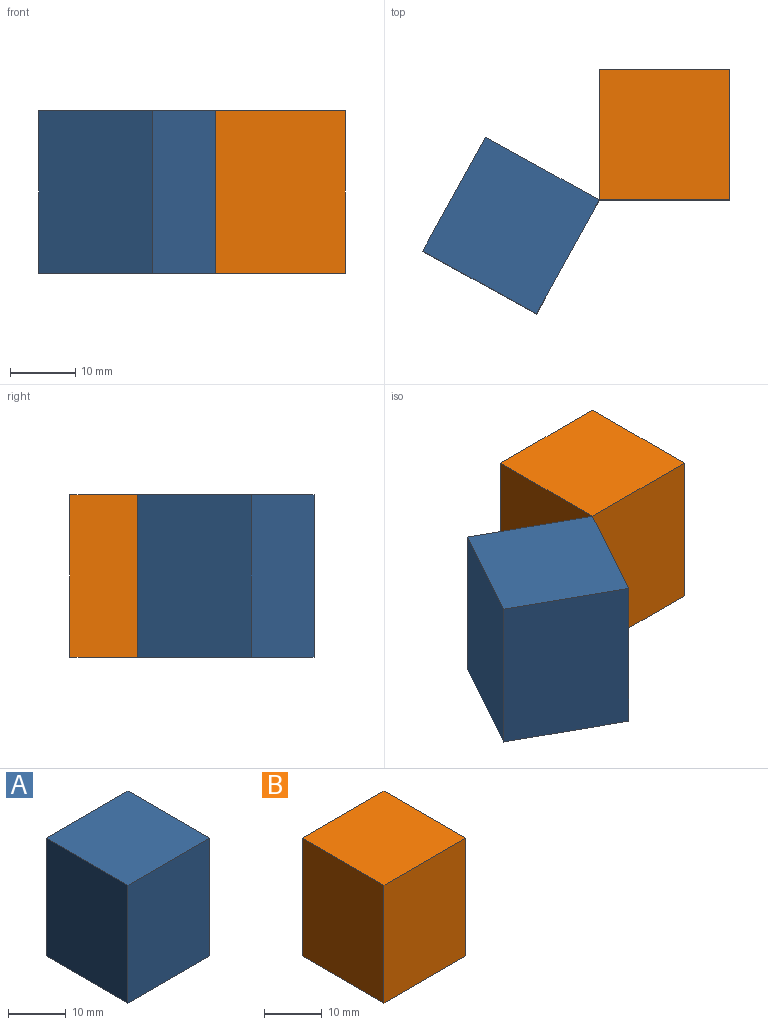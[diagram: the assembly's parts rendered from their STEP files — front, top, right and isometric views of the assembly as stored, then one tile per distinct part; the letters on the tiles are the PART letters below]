
ASSEMBLY  parts=2 mates=1
PART A: 6 faces, bbox 20x20x25 mm
  f0: plane 25x20mm, normal (1,0,0), area 500mm2, adj f1,f3,f4,f5
  f1: plane 25x20mm, normal (0,1,0), area 500mm2, adj f0,f2,f4,f5
  f2: plane 25x20mm, normal (-1,0,0), area 500mm2, adj f1,f3,f4,f5
  f3: plane 25x20mm, normal (0,-1,0), area 500mm2, adj f0,f2,f4,f5
  f4: plane 20x20mm, normal (0,0,1), area 400mm2, adj f0,f1,f2,f3
  f5: plane 20x20mm, normal (0,0,-1), area 400mm2, adj f0,f1,f2,f3
PART B: 6 faces, bbox 20x20x25 mm
  f0: plane 25x20mm, normal (1,0,0), area 500mm2, adj f1,f3,f4,f5
  f1: plane 25x20mm, normal (0,1,0), area 500mm2, adj f0,f2,f4,f5
  f2: plane 25x20mm, normal (-1,0,0), area 500mm2, adj f1,f3,f4,f5
  f3: plane 25x20mm, normal (0,-1,0), area 500mm2, adj f0,f2,f4,f5
  f4: plane 20x20mm, normal (0,0,-1), area 400mm2, adj f0,f1,f2,f3
  f5: plane 20x20mm, normal (0,0,1), area 400mm2, adj f0,f1,f2,f3
PLACE A rot(axis=(0,0,-1),28.9deg) t=(-4.7,16.35,1.96)mm
PLACE B t=(18.88,30.28,26.96)mm fixed
MATE revolute A.f4 <-> B.f5  axis (0,0,1) through (8.88,20.28,26.96)mm
